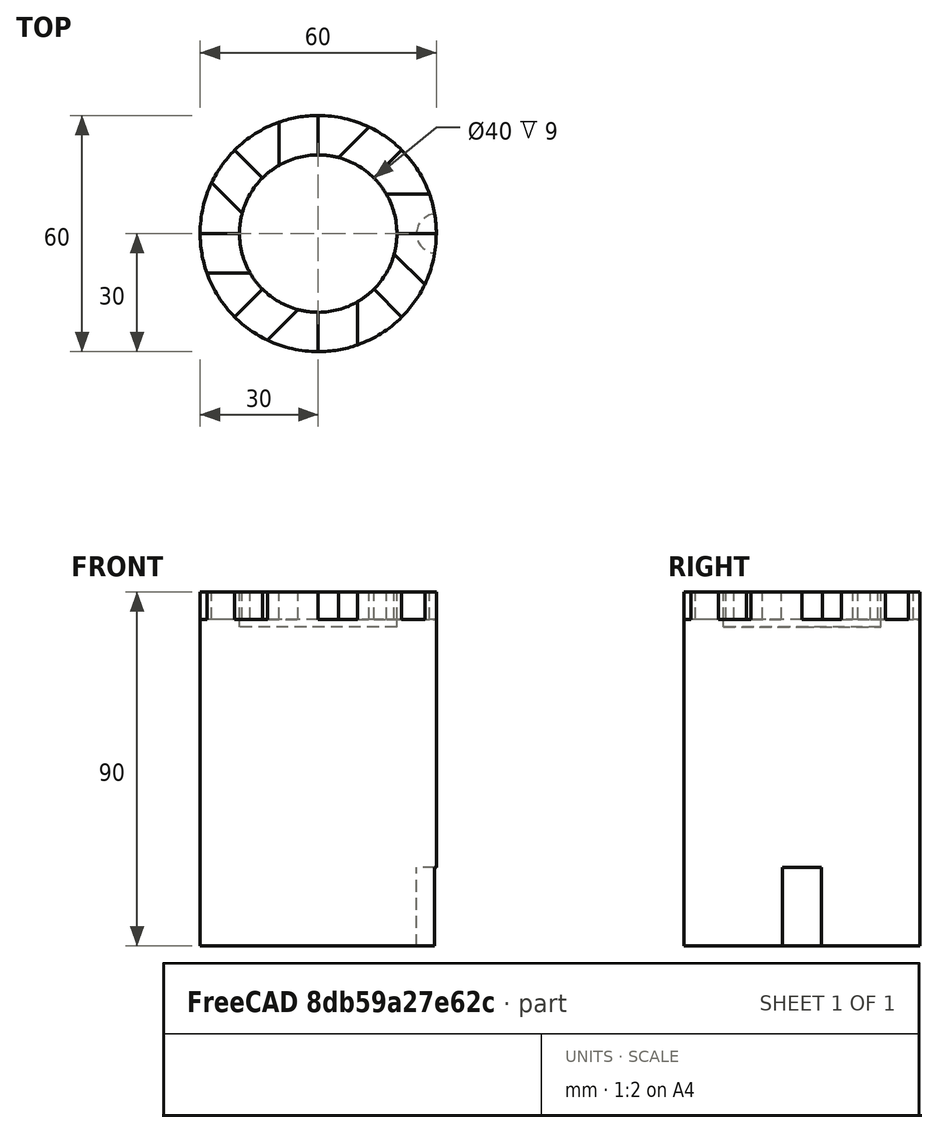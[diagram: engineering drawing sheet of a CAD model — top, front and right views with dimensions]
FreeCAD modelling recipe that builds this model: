
FCSTD DOCUMENT  (FreeCAD 0.18R16146 (Git))
Label: torre_dani
License: All rights reserved
LicenseURL: http://en.wikipedia.org/wiki/All_rights_reserved
objects: Part::Cylinder×3, Part::Cut×3, Part::Box×1, Part::FeaturePython×1
note: 8 computed .brp shape members not serialized (recipe doc carries the construction recipe); baked Part::Feature solids carry a one-line shape summary decoded from their .brp

FEATURE [Part::Cylinder] Cylinder  label="Cilindro"
  Angle = 360
  AttacherType = Attacher::AttachEngine3D
  Height = 90
  Radius = 30
FEATURE [Part::Cylinder] Cylinder001  label="Cilindro"
  Angle = 360
  AttacherType = Attacher::AttachEngine3D
  Height = 10
  Placement = pos=(0,0,81) rot=(0,0,1;0rad)
  Radius = 20
FEATURE [Part::Cut] Cut
  Base = -> Cylinder
  Refine = true
  Tool = -> Cylinder001
FEATURE [Part::Box] Box  label="Cubo"
  AttacherType = Attacher::AttachEngine3D
  Height = 10
  Length = 20
  Placement = pos=(13,0,83) rot=(0,0,1;0rad)
  Width = 10
FEATURE [Part::FeaturePython] Array  # Draft array (typed FeaturePython)
  Angle = 360
  ArrayType = 1
  Axis = (0,0,1)
  Base = -> Box
  Center = (0,0,0)
  Fuse = false
  IntervalAxis = (0,0,0)
  IntervalX = (1,0,0)
  IntervalY = (0,1,0)
  IntervalZ = (0,0,1)
  NumberPolar = 8
  NumberX = 2
  NumberY = 2
  NumberZ = 1
FEATURE [Part::Cut] Cut001
  Base = -> Cut
  Refine = true
  Tool = -> Array
FEATURE [Part::Cylinder] Cylinder002  label="Cilindro"
  Angle = 360
  AttacherType = Attacher::AttachEngine3D
  Height = 20
  Placement = pos=(30,0,0) rot=(0,0,1;0rad)
  Radius = 5
FEATURE [Part::Cut] Cut002
  Base = -> Cut001
  Refine = true
  Tool = -> Cylinder002
